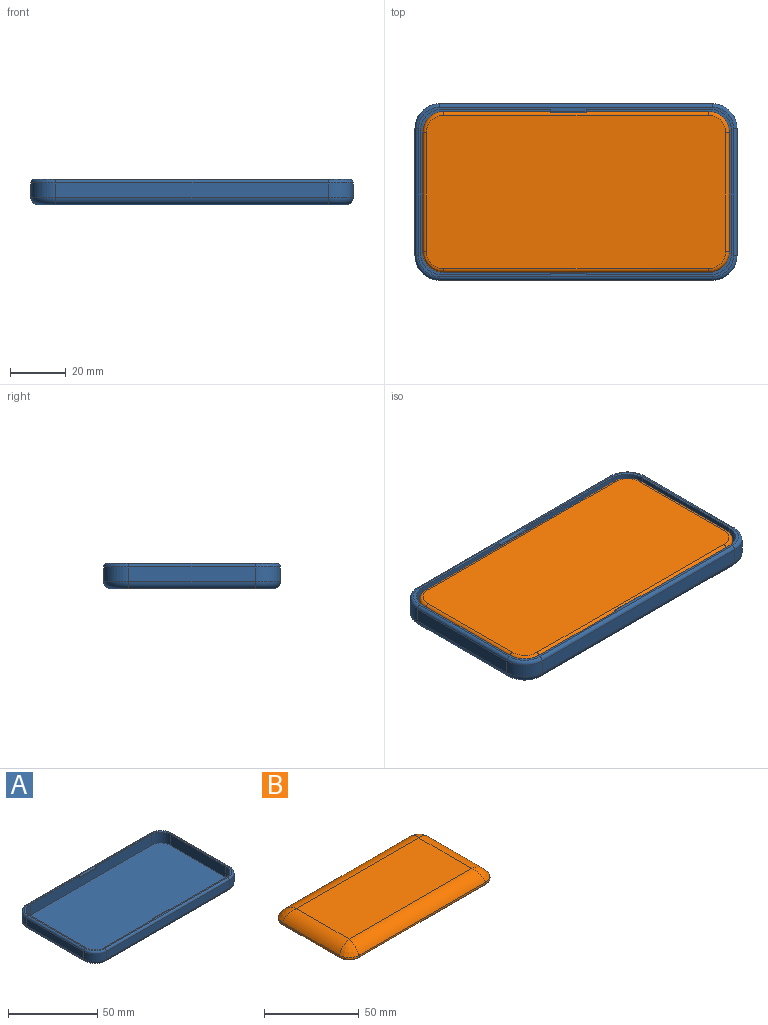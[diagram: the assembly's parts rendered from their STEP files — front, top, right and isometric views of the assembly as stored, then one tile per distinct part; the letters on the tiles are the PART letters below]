
ASSEMBLY  parts=2 mates=1
PART A: 46 faces, bbox 116.8x64.7x9 mm
  f0: plane 96.06x7.5mm, normal (0,1,0), area 702.7mm2, adj f8,f14,f16,f18,f24,f25,f27
  f1: cylinder r=8.89mm len=8.89mm, axis (0,0,-1), area 72.5mm2, adj f2,f15,f34,f40
  f2: plane 97.52x5.19mm, normal (0,-1,0), area 506.1mm2, adj f1,f3,f32,f42
  f3: cylinder r=8.89mm len=8.89mm, axis (0,0,-1), area 72.5mm2, adj f2,f4,f30,f44
  f4: plane 45.42x5.19mm, normal (1,0,0), area 235.7mm2, adj f3,f5,f31,f45
  f5: cylinder r=8.89mm len=8.89mm, axis (0,0,-1), area 72.5mm2, adj f4,f6,f33,f43
  f6: plane 97.52x5.19mm, normal (0,1,0), area 506.1mm2, adj f5,f7,f35,f41
  f7: cylinder r=8.89mm len=8.89mm, axis (0,0,-1), area 72.5mm2, adj f6,f15,f37,f39
  f8: cylinder r=7.62mm len=7.62mm, axis (0,0,-1), area 89.8mm2, adj f0,f9,f16,f18
  f9: plane 43.96x7.5mm, normal (1,0,0), area 329.7mm2, adj f8,f10,f16,f18
  f10: cylinder r=7.62mm len=7.62mm, axis (0,0,-1), area 89.8mm2, adj f9,f11,f16,f18
  f11: plane 96.06x7.5mm, normal (0,-1,0), area 702.7mm2, adj f10,f12,f16,f18,f19,f20,f22
  f12: cylinder r=7.62mm len=7.62mm, axis (0,0,-1), area 89.8mm2, adj f11,f13,f16,f18
  f13: plane 43.96x7.5mm, normal (-1,0,0), area 329.7mm2, adj f12,f14,f16,f18
  f14: cylinder r=7.62mm len=7.62mm, axis (0,0,-1), area 89.8mm2, adj f0,f13,f16,f18
  f15: plane 45.42x5.19mm, normal (-1,0,0), area 235.7mm2, adj f1,f7,f36,f38
  f16: plane 112.76x60.66mm, normal (0,0,1), area 269.4mm2, adj f0,f8,f9,f10,f11,f12,f13,f14
  f17: plane 110.22x58.12mm, normal (0,0,-1), area 6371.4mm2, adj f30,f31,f32,f33,f34,f35,f36,f37
  f18: plane 111.3x59.2mm, normal (0,0,1), area 6539.1mm2, adj f0,f8,f9,f10,f11,f12,f13,f14
  f19: plane 1.4x1.27mm, normal (1,0,0), area 1.1mm2, adj f11,f16,f21,f22,f23
  f20: plane 1.4x1.27mm, normal (-1,0,0), area 1.1mm2, adj f11,f16,f21,f22,f23
  f21: cylinder r=0.76mm len=12.7mm, axis (-1,0,0), area 15.2mm2, adj f19,f20,f22,f23
  f22: plane 12.7x0.51mm, normal (0,-0.71,-0.71), area 9.1mm2, adj f11,f19,f20,f21
  f23: cylinder r=0.51mm len=12.7mm, axis (1,0,0), area 4.7mm2, adj f16,f19,f20,f21
  f24: plane 1.4x0.76mm, normal (1,0,0), area 0.7mm2, adj f0,f16,f26,f27,f28,f29
  f25: plane 1.4x0.76mm, normal (-1,0,0), area 0.7mm2, adj f0,f16,f26,f27,f28,f29
  f26: plane 12.7x0.07mm, normal (0,1,0), area 0.9mm2, adj f24,f25,f28,f29
  f27: plane 12.7x0.51mm, normal (0,0.71,-0.71), area 9.1mm2, adj f0,f24,f25,f28
  f28: cylinder r=0.76mm len=12.7mm, axis (1,0,0), area 8.1mm2, adj f24,f25,f26,f27
  f29: cylinder r=0.25mm len=12.7mm, axis (1,0,0), area 5.1mm2, adj f16,f24,f25,f26
  f30: torus R=6.35mm, axis (0,0,1), area 49.9mm2, adj f3,f17,f31,f32
  f31: cylinder r=2.54mm len=45.42mm, axis (0,1,0), area 181.2mm2, adj f4,f17,f30,f33
  f32: cylinder r=2.54mm len=97.52mm, axis (1,0,0), area 389.1mm2, adj f2,f17,f30,f34
  f33: torus R=6.35mm, axis (0,0,1), area 49.9mm2, adj f5,f17,f31,f35
  f34: torus R=6.35mm, axis (0,0,1), area 49.9mm2, adj f1,f17,f32,f36
  f35: cylinder r=2.54mm len=97.52mm, axis (-1,0,0), area 389.1mm2, adj f6,f17,f33,f37
  f36: cylinder r=2.54mm len=45.42mm, axis (0,-1,0), area 181.2mm2, adj f15,f17,f34,f37
  f37: torus R=6.35mm, axis (0,0,1), area 49.9mm2, adj f7,f17,f35,f36
  f38: cylinder r=1.27mm len=45.42mm, axis (0,1,0), area 90.6mm2, adj f15,f16,f39,f40
  f39: torus R=7.62mm, axis (0,0,1), area 26.4mm2, adj f7,f16,f38,f41
  f40: torus R=7.62mm, axis (0,0,1), area 26.4mm2, adj f1,f16,f38,f42
  f41: cylinder r=1.27mm len=97.52mm, axis (1,0,0), area 194.5mm2, adj f6,f16,f39,f43
  f42: cylinder r=1.27mm len=97.52mm, axis (-1,0,0), area 194.5mm2, adj f2,f16,f40,f44
  f43: torus R=7.62mm, axis (0,0,1), area 26.4mm2, adj f5,f16,f41,f45
  f44: torus R=7.62mm, axis (0,0,1), area 26.4mm2, adj f3,f16,f42,f45
  f45: cylinder r=1.27mm len=45.42mm, axis (0,-1,0), area 90.6mm2, adj f4,f16,f43,f44
PART B: 18 faces, bbox 111.4x59.3x7.2 mm
  f0: plane 91.46x39.36mm, normal (0,0,1), area 3600.1mm2, adj f2,f5,f6,f9
  f1: plane 107.1x55mm, normal (0,0,-1), area 5857.6mm2, adj f10,f11,f12,f13,f14,f15,f16,f17
  f2: cylinder r=10.16mm len=42.52mm, axis (0,-1,0), area 447.1mm2, adj f0,f3,f4,f15
  f3: bspline ~9.36x9.36mm, area 69.5mm2, adj f2,f5,f17
  f4: bspline ~9.36x9.36mm, area 69.5mm2, adj f2,f6,f13
  f5: cylinder r=10.16mm len=94.62mm, axis (1,0,0), area 1016.1mm2, adj f0,f3,f7,f16
  f6: cylinder r=10.16mm len=94.62mm, axis (1,0,0), area 1016.1mm2, adj f0,f4,f8,f11
  f7: bspline ~9.36x9.36mm, area 69.5mm2, adj f5,f9,f14
  f8: bspline ~9.36x9.36mm, area 69.5mm2, adj f6,f9,f10
  f9: cylinder r=10.16mm len=42.52mm, axis (0,-1,0), area 447.1mm2, adj f0,f7,f8,f12
  f10: bspline ~8.96x8.96mm, area 29.9mm2, adj f1,f8,f11,f12
  f11: cylinder r=1.27mm len=94.62mm, axis (1,0,0), area 248.4mm2, adj f1,f6,f10,f13
  f12: cylinder r=1.27mm len=42.52mm, axis (0,-1,0), area 111.6mm2, adj f1,f9,f10,f14
  f13: bspline ~8.96x8.96mm, area 29.9mm2, adj f1,f4,f11,f15
  f14: bspline ~8.96x8.96mm, area 29.9mm2, adj f1,f7,f12,f16
  f15: cylinder r=1.27mm len=42.52mm, axis (0,-1,0), area 111.6mm2, adj f1,f2,f13,f17
  f16: cylinder r=1.27mm len=94.62mm, axis (1,0,0), area 248.4mm2, adj f1,f5,f14,f17
  f17: bspline ~8.96x8.96mm, area 29.9mm2, adj f1,f3,f15,f16
PLACE A t=(-3.6,10.76,13.22)mm fixed
PLACE B rot(axis=(1,0,0),180deg) t=(-3.6,10.76,21.92)mm
MATE planar A.f18 <-> B.f0  axis (0,0,1) through (-3.6,10.76,14.72)mm
